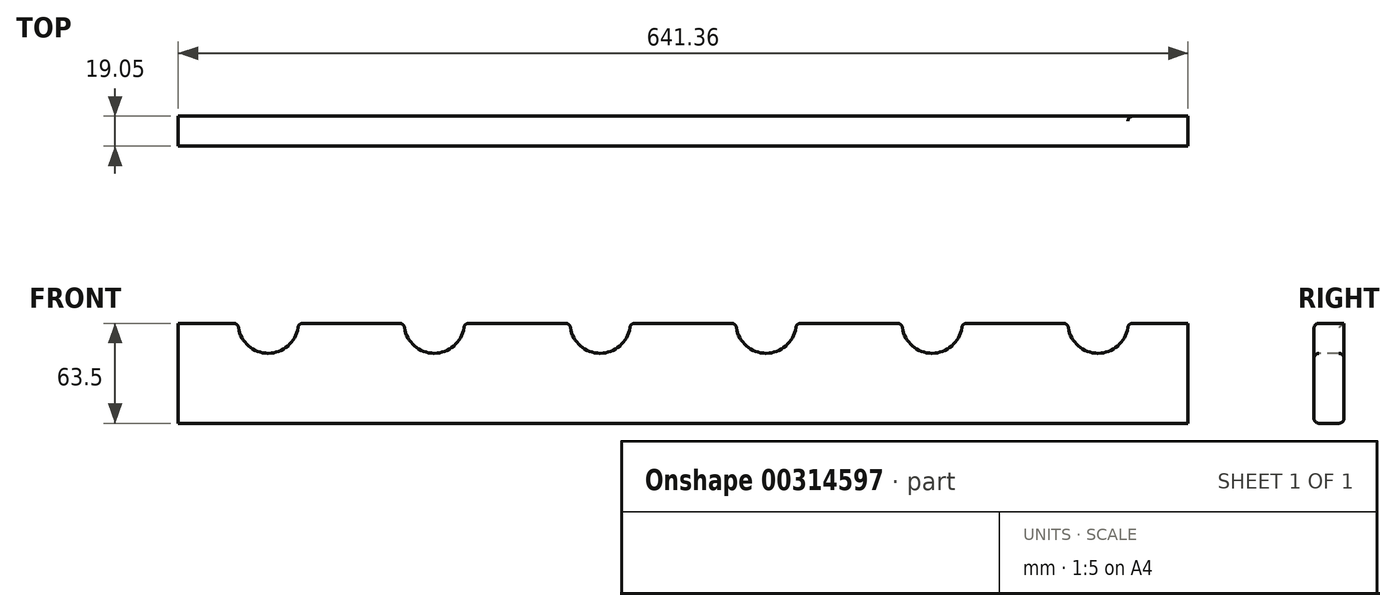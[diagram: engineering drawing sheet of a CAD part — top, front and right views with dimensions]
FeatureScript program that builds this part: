
annotation { "Feature Type Name" : "Feature", "Feature Type Description" : "" }
export const myFeature = defineFeature(function(context is Context, id is Id, definition is map)
    precondition{}
    {
        {
            var Q0;
            Q0=qCreatedBy(makeId("Front.planeOp"),FACE);
            var sketch = newSketch(context, id + "F0", { "sketchPlane" : qUnion([Q0])});
            skLineSegment(sketch, "E0.top", {"start": v(-320.68, -31.75) * mm, "end": v(320.68, -31.75) * mm});
            skLineSegment(sketch, "E0.left", {"start": v(-320.68, 31.75) * mm, "end": v(-320.68, -31.75) * mm});
            skLineSegment(sketch, "E0.right", {"start": v(320.68, 31.75) * mm, "end": v(320.68, -31.75) * mm});
            skCircle(sketch, "E1", {"center": v(-263.53, 31.75) * mm, "radius": 19.05 * mm});
            skCircle(sketch, "E2", {"center": v(-52.7, 31.75) * mm, "radius": 19.05 * mm});
            skLineSegment(sketch, "E3", {"start": v(-320.68, -31.75) * mm, "end": v(320.67, 31.75) * mm, "construction": true});
            skCircle(sketch, "E4", {"center": v(52.7, 31.75) * mm, "radius": 19.05 * mm});
            skCircle(sketch, "E5", {"center": v(158.12, 31.75) * mm, "radius": 19.05 * mm});
            skCircle(sketch, "E6", {"center": v(263.53, 31.75) * mm, "radius": 19.05 * mm});
            skLineSegment(sketch, "E7", {"start": v(-320.68, 31.75) * mm, "end": v(-263.53, 31.75) * mm});
            skLineSegment(sketch, "E8", {"start": v(-158.12, 31.75) * mm, "end": v(-52.7, 31.75) * mm});
            skLineSegment(sketch, "E9", {"start": v(-52.7, 31.75) * mm, "end": v(52.7, 31.75) * mm});
            skLineSegment(sketch, "E10", {"start": v(52.7, 31.75) * mm, "end": v(158.12, 31.75) * mm});
            skLineSegment(sketch, "E11", {"start": v(158.12, 31.75) * mm, "end": v(263.53, 31.75) * mm});
            skLineSegment(sketch, "E12", {"start": v(263.53, 31.75) * mm, "end": v(320.68, 31.75) * mm});
            skCircle(sketch, "E13", {"center": v(-158.12, 31.75) * mm, "radius": 19.05 * mm});
            skLineSegment(sketch, "E14", {"start": v(-263.53, 31.75) * mm, "end": v(-158.12, 31.75) * mm});
            skSolve(sketch);
        }
        {
            var Q0;
            Q0=makeQuery(id+"F0.imprint","IMPRINT",FACE,{"disambiguationData":[TD([[makeQuery(id+"F0.imprint","IMPRINT",EDGE,{"derivedFrom":sQuery(id+"F0.wireOp",EDGE,"E0.top")}),1.0]])]});
            extrude(context, id + "F1", {"entities" : qUnion([Q0]), "oppositeDirection" : true, "depth" : 19.05 * mm});
        }
        {
            var Q0;
            Q0=makeQuery(id+"F1.opExtrude","SWEPT_FACE",FACE,{"disambiguationData":[OSD([sQuery(id+"F0.wireOp",EDGE,"E1")])]});
            var Q1;
            Q1=makeQuery(id+"F1.opExtrude","CAP_EDGE",EDGE,{"disambiguationData":[OSD([sQuery(id+"F0.wireOp",EDGE,"E7")])],"isStart":true});
            var Q2;
            Q2=makeQuery(id+"F1.opExtrude","CAP_EDGE",EDGE,{"disambiguationData":[OSD([sQuery(id+"F0.wireOp",EDGE,"E7")])],"isStart":false});
            var Q3;
            Q3=makeQuery(id+"F1.opExtrude","SWEPT_FACE",FACE,{"disambiguationData":[OSD([sQuery(id+"F0.wireOp",EDGE,"E14")])]});
            var Q4;
            Q4=makeQuery(id+"F1.opExtrude","SWEPT_FACE",FACE,{"disambiguationData":[OSD([sQuery(id+"F0.wireOp",EDGE,"E13")])]});
            var Q5;
            Q5=makeQuery(id+"F1.opExtrude","SWEPT_FACE",FACE,{"disambiguationData":[OSD([sQuery(id+"F0.wireOp",EDGE,"E8")])]});
            var Q6;
            Q6=makeQuery(id+"F1.opExtrude","SWEPT_FACE",FACE,{"disambiguationData":[OSD([sQuery(id+"F0.wireOp",EDGE,"E2")])]});
            var Q7;
            Q7=makeQuery(id+"F1.opExtrude","SWEPT_FACE",FACE,{"disambiguationData":[OSD([sQuery(id+"F0.wireOp",EDGE,"E9")])]});
            var Q8;
            Q8=makeQuery(id+"F1.opExtrude","SWEPT_FACE",FACE,{"disambiguationData":[OSD([sQuery(id+"F0.wireOp",EDGE,"E4")])]});
            var Q9;
            Q9=makeQuery(id+"F1.opExtrude","SWEPT_FACE",FACE,{"disambiguationData":[OSD([sQuery(id+"F0.wireOp",EDGE,"E10")])]});
            var Q10;
            Q10=makeQuery(id+"F1.opExtrude","SWEPT_FACE",FACE,{"disambiguationData":[OSD([sQuery(id+"F0.wireOp",EDGE,"E5")])]});
            var Q11;
            Q11=makeQuery(id+"F1.opExtrude","SWEPT_FACE",FACE,{"disambiguationData":[OSD([sQuery(id+"F0.wireOp",EDGE,"E11")])]});
            var Q12;
            Q12=makeQuery(id+"F1.opExtrude","SWEPT_FACE",FACE,{"disambiguationData":[OSD([sQuery(id+"F0.wireOp",EDGE,"E6")])]});
            var Q13;
            Q13=makeQuery(id+"F1.opExtrude","CAP_EDGE",EDGE,{"disambiguationData":[OSD([sQuery(id+"F0.wireOp",EDGE,"E12")])],"isStart":true});
            fillet(context, id + "F2", {"entities" : qUnion([Q0, Q1, Q2, Q3, Q4, Q5, Q6, Q7, Q8, Q9, Q10, Q11, Q12, Q13]), "radius" : 3.17 * mm, "tangentPropagation" : true, "allowEdgeOverflow" : false});
        }
        {
            var Q0;
            Q0=makeQuery(id+"F1.opExtrude","CAP_EDGE",EDGE,{"disambiguationData":[OSD([sQuery(id+"F0.wireOp",EDGE,"E0.top")])],"isStart":true});
            var Q1;
            Q1=makeQuery(id+"F1.opExtrude","CAP_EDGE",EDGE,{"disambiguationData":[OSD([sQuery(id+"F0.wireOp",EDGE,"E0.top")])],"isStart":false});
            fillet(context, id + "F3", {"entities" : qUnion([Q0, Q1]), "radius" : 3.17 * mm, "tangentPropagation" : true, "allowEdgeOverflow" : false});
        }
    });
